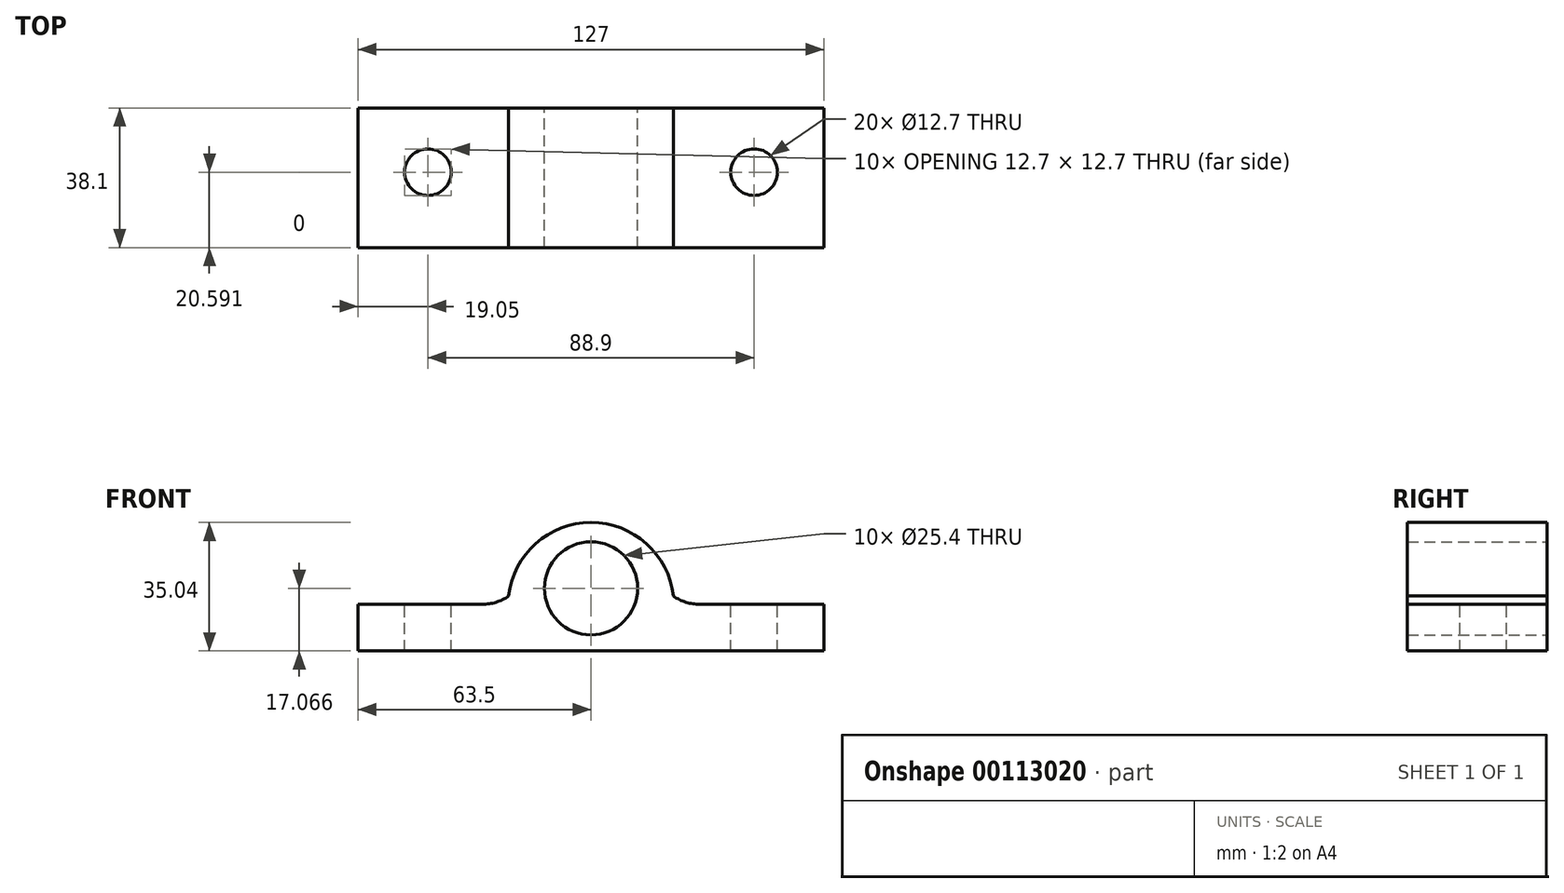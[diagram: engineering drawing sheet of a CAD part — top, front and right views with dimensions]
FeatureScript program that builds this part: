
annotation { "Feature Type Name" : "Feature", "Feature Type Description" : "" }
export const myFeature = defineFeature(function(context is Context, id is Id, definition is map)
    precondition{}
    {
        {
            var Q0;
            Q0=qCreatedBy(makeId("Front.planeOp"),FACE);
            var sketch = newSketch(context, id + "F0", { "sketchPlane" : qUnion([Q0])});
            skLineSegment(sketch, "E0", {"start": v(0, 0) * mm, "end": v(-63.5, 0) * mm});
            skLineSegment(sketch, "E1", {"start": v(63.5, 0) * mm, "end": v(0, 0) * mm});
            skLineSegment(sketch, "E2", {"start": v(-63.5, 12.7) * mm, "end": v(-63.5, 0) * mm});
            skLineSegment(sketch, "E3", {"start": v(-29.66, 12.7) * mm, "end": v(-63.5, 12.7) * mm});
            skLineSegment(sketch, "E4", {"start": v(63.5, 0) * mm, "end": v(63.5, 12.7) * mm});
            skLineSegment(sketch, "E5", {"start": v(63.5, 12.7) * mm, "end": v(29.66, 12.7) * mm});
            skCircle(sketch, "E6", {"center": v(0, 17.07) * mm, "radius": 12.7 * mm});
            skPoint(sketch, "E7.visualSharp", {"position": v(-25.4, 12.7) * mm});
            skArc(sketch, "E7.filletArc", {"start": v(-29.66, 12.7) * mm, "mid": v(-25.89, 13.28) * mm, "end": v(-22.45, 14.95) * mm});
            skPoint(sketch, "E8.visualSharp", {"position": v(25.4, 12.7) * mm});
            skArc(sketch, "E8.filletArc", {"start": v(22.45, 14.95) * mm, "mid": v(25.89, 13.28) * mm, "end": v(29.66, 12.7) * mm});
            skArc(sketch, "E9", {"start": v(22.45, 14.95) * mm, "mid": v(0, 35.04) * mm, "end": v(-22.45, 14.95) * mm});
            skSolve(sketch);
        }
        {
            var Q0;
            Q0 = qSketchRegion(id + "F0", true);
            extrude(context, id + "F1", {"entities" : qUnion([Q0]), "depth" : 38.1 * mm});
        }
        {
            var Q0;
            Q0=makeQuery(id+"F1.opExtrude","SWEPT_FACE",FACE,{"disambiguationData":[OSD([sQuery(id+"F0.wireOp",EDGE,"E3")])]});
            var sketch = newSketch(context, id + "F2", { "sketchPlane" : qUnion([Q0])});
            skPoint(sketch, "E10.centerSnap0", {"position": v(-46.58, 0) * mm});
            skCircle(sketch, "E11", {"center": v(-44.45, -17.5) * mm, "radius": 6.35 * mm});
            skCircle(sketch, "E12.MirrorC", {"center": v(44.45, -17.5) * mm, "radius": 6.35 * mm});
            skSolve(sketch);
        }
        {
            var Q0;
            Q0 = qSketchRegion(id + "F2", true);
            extrude(context, id + "F3", {"entities" : qUnion([Q0]), "operationType" : NewBodyOperationType.REMOVE, "endBound" : BoundingType.SYMMETRIC, "oppositeDirection" : true, "depth" : 25.4 * mm});
        }
    });
